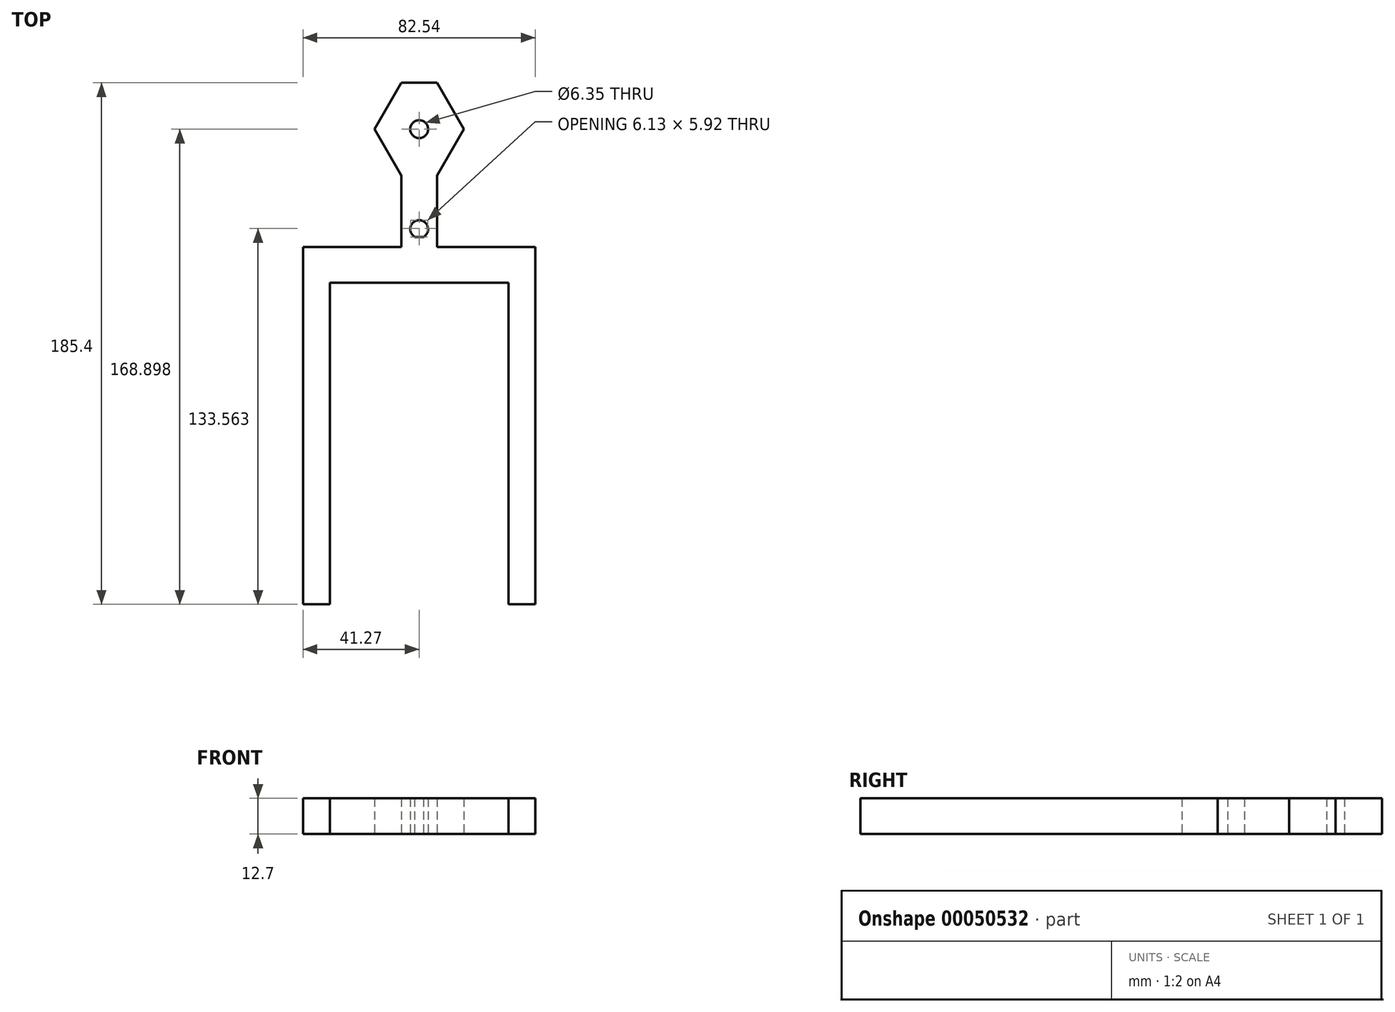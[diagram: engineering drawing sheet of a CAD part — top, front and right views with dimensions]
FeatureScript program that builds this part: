
annotation { "Feature Type Name" : "Feature", "Feature Type Description" : "" }
export const myFeature = defineFeature(function(context is Context, id is Id, definition is map)
    precondition{}
    {
        {
            var Q0;
            Q0=qCreatedBy(makeId("Top.planeOp"),FACE);
            var sketch = newSketch(context, id + "F0", { "sketchPlane" : qUnion([Q0])});
            skLineSegment(sketch, "E0.rect.bottom", {"start": v(6.35, -6.35) * mm, "end": v(-6.35, -6.35) * mm});
            skLineSegment(sketch, "E0.rect.top", {"start": v(6.35, 6.35) * mm, "end": v(-6.35, 6.35) * mm});
            skLineSegment(sketch, "E0.rect.left", {"start": v(6.35, -6.35) * mm, "end": v(6.35, 6.35) * mm});
            skLineSegment(sketch, "E0.rect.right", {"start": v(-6.35, -6.35) * mm, "end": v(-6.35, 6.35) * mm});
            skPoint(sketch, "E0.rect.middle", {"position": v(0, 0) * mm});
            skPoint(sketch, "E1.endSnap0", {"position": v(0, 6.35) * mm});
            skCircle(sketch, "E2", {"center": v(0, 0) * mm, "radius": 3.18 * mm});
            skLineSegment(sketch, "E3", {"start": v(-6.35, 6.35) * mm, "end": v(-6.35, 19.05) * mm});
            skLineSegment(sketch, "E4", {"start": v(-6.35, -6.35) * mm, "end": v(-41.28, -6.35) * mm});
            skLineSegment(sketch, "E5", {"start": v(-41.28, -6.35) * mm, "end": v(-41.27, -133.35) * mm});
            skLineSegment(sketch, "E6", {"start": v(-41.27, -133.35) * mm, "end": v(-31.75, -133.35) * mm});
            skLineSegment(sketch, "E7", {"start": v(-31.75, -133.35) * mm, "end": v(-31.75, -19.05) * mm});
            skLineSegment(sketch, "E8", {"start": v(-31.75, -19.05) * mm, "end": v(0, -19.05) * mm});
            skLineSegment(sketch, "E9", {"start": v(0, 59.1) * mm, "end": v(0, -42.89) * mm, "construction": true});
            skPoint(sketch, "E9.startSnap0", {"position": v(0, -6.35) * mm});
            skLineSegment(sketch, "E10", {"start": v(-1.59, -2.75) * mm, "end": v(1.59, -2.75) * mm});
            skLineSegment(sketch, "E11", {"start": v(-39.44, 0) * mm, "end": v(34.43, 0) * mm, "construction": true});
            skLineSegment(sketch, "E12", {"start": v(-6.35, 19.05) * mm, "end": v(-15.87, 35.55) * mm});
            skLineSegment(sketch, "E13", {"start": v(-15.88, 35.55) * mm, "end": v(-6.35, 52.05) * mm});
            skLineSegment(sketch, "E14", {"start": v(-48.92, 35.55) * mm, "end": v(48.92, 35.55) * mm, "construction": true});
            skLineSegment(sketch, "E15", {"start": v(-6.35, 52.05) * mm, "end": v(0, 52.05) * mm});
            skLineSegment(sketch, "E16.MirrorCS", {"start": v(6.35, 6.35) * mm, "end": v(6.35, 19.05) * mm});
            skLineSegment(sketch, "E17.MirrorCS", {"start": v(6.35, 19.05) * mm, "end": v(15.88, 35.55) * mm});
            skLineSegment(sketch, "E18.MirrorCS", {"start": v(6.35, 52.05) * mm, "end": v(0, 52.05) * mm});
            skLineSegment(sketch, "E19.MirrorCS", {"start": v(15.88, 35.55) * mm, "end": v(6.35, 52.05) * mm});
            skLineSegment(sketch, "E20.MirrorCS", {"start": v(6.35, -6.35) * mm, "end": v(41.28, -6.35) * mm});
            skLineSegment(sketch, "E21.MirrorCS", {"start": v(41.27, -133.35) * mm, "end": v(31.75, -133.35) * mm});
            skLineSegment(sketch, "E22.MirrorCS", {"start": v(41.28, -6.35) * mm, "end": v(41.28, -133.35) * mm});
            skLineSegment(sketch, "E23.MirrorCS", {"start": v(31.75, -19.05) * mm, "end": v(0, -19.05) * mm});
            skLineSegment(sketch, "E24.MirrorCS", {"start": v(31.75, -133.35) * mm, "end": v(31.75, -19.05) * mm});
            skCircle(sketch, "E25", {"center": v(0, 35.55) * mm, "radius": 3.18 * mm});
            skSolve(sketch);
        }
        {
            var Q0;
            Q0 = qSketchRegion(id + "F0", true);
            var Q1;
            {var subQ0=sQuery(id+"F0.wireOp",EDGE,"E10");Q1=makeQuery(id+"F0.imprint","IMPRINT",FACE,{"disambiguationData":[TD([[makeQuery(id+"F0.imprint","IMPRINT",EDGE,{"derivedFrom":subQ0}),-1.0]])]});}
            extrude(context, id + "F1", {"entities" : qUnion([Q0, Q1]), "depth" : 12.7 * mm});
        }
    });
